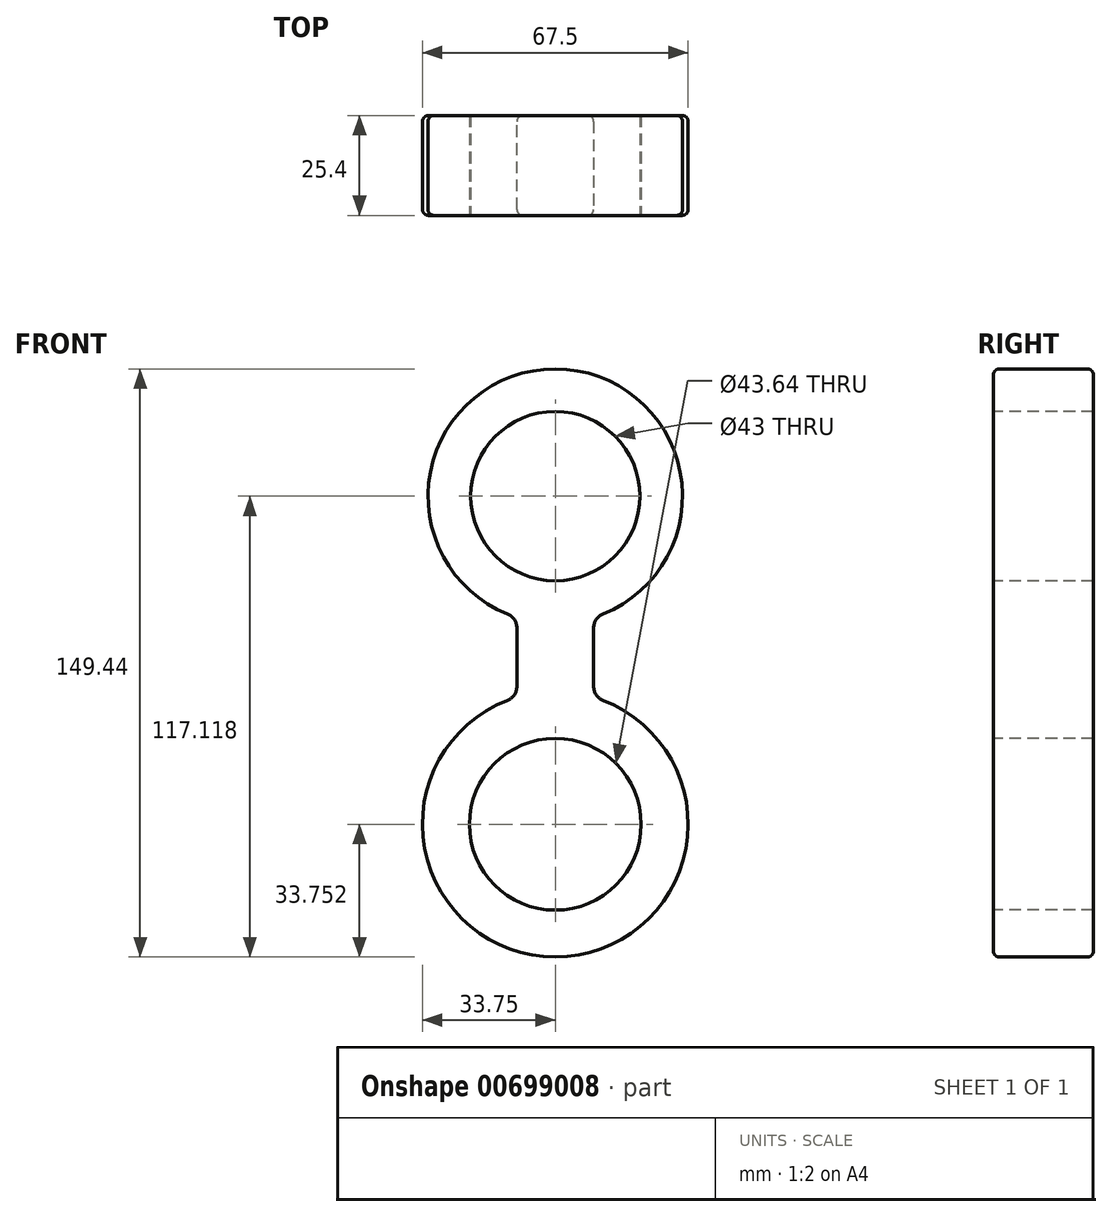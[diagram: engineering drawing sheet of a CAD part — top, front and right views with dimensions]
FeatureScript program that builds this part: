
annotation { "Feature Type Name" : "Feature", "Feature Type Description" : "" }
export const myFeature = defineFeature(function(context is Context, id is Id, definition is map)
    precondition{}
    {
        {
            var Q0;
            Q0=qCreatedBy(makeId("Front.planeOp"),FACE);
            var sketch = newSketch(context, id + "F0", { "sketchPlane" : qUnion([Q0])});
            skCircle(sketch, "E0", {"center": v(0, -42.15) * mm, "radius": 33.75 * mm});
            skCircle(sketch, "E1", {"center": v(0, -42.15) * mm, "radius": 21.82 * mm});
            skSolve(sketch);
        }
        {
            var Q0;
            Q0=makeQuery(id+"F0.imprint","IMPRINT",FACE,{"disambiguationData":[TD([[makeQuery(id+"F0.imprint","IMPRINT",EDGE,{"derivedFrom":sQuery(id+"F0.wireOp",EDGE,"E0")}),1.0]])]});
            var sketch = newSketch(context, id + "F1", { "sketchPlane" : qUnion([Q0])});
            skSolve(sketch);
        }
        {
            var Q0;
            Q0=makeQuery(id+"F1.imprint","IMPRINT",FACE,{"disambiguationData":[TD([[makeQuery(id+"F1.imprint","IMPRINT",EDGE,{"derivedFrom":makeQuery(id+"F0.imprint","IMPRINT",EDGE,{"derivedFrom":sQuery(id+"F0.wireOp",EDGE,"E0")})}),1.0]])]});
            var sketch = newSketch(context, id + "F2", { "sketchPlane" : qUnion([Q0])});
            skLineSegment(sketch, "E2.bottom", {"start": v(9.75, 16.05) * mm, "end": v(-9.75, 16.05) * mm});
            skLineSegment(sketch, "E2.top", {"start": v(9.75, -16.05) * mm, "end": v(-9.75, -16.05) * mm});
            skLineSegment(sketch, "E2.left", {"start": v(9.75, 16.05) * mm, "end": v(9.75, -16.05) * mm});
            skLineSegment(sketch, "E2.right", {"start": v(-9.75, 16.05) * mm, "end": v(-9.75, -16.05) * mm});
            skPoint(sketch, "E2.middle", {"position": v(0, 0) * mm});
            skSolve(sketch);
        }
        {
            var Q0;
            {var subQ1=sQuery(id+"F2.wireOp",EDGE,"E2.top");Q0=makeQuery(id+"F2.imprint","IMPRINT",FACE,{"disambiguationData":[TD([[makeQuery(id+"F2.imprint","IMPRINT",EDGE,{"derivedFrom":subQ1}),1.0]])]});}
            var Q1;
            {var subQ0=sQuery(id+"F2.wireOp",EDGE,"E2.bottom");Q1=makeQuery(id+"F2.imprint","IMPRINT",FACE,{"disambiguationData":[TD([[makeQuery(id+"F2.imprint","IMPRINT",EDGE,{"derivedFrom":subQ0}),1.0]])]});}
            var Q2;
            {var subQ0=sQuery(id+"F2.wireOp",EDGE,"E2.top");Q2=makeQuery(id+"F2.imprint","IMPRINT",FACE,{"disambiguationData":[TD([[makeQuery(id+"F2.imprint","IMPRINT",EDGE,{"derivedFrom":subQ0}),-1.0]])]});}
            extrude(context, id + "F3", {"entities" : qUnion([Q0, Q1, Q2]), "oppositeDirection" : true, "depth" : 25.4 * mm, "offsetDistance" : 25.4 * mm});
        }
        {
            var Q0;
            Q0=qCreatedBy(makeId("Front.planeOp"),FACE);
            var sketch = newSketch(context, id + "F4", { "sketchPlane" : qUnion([Q0])});
            skCircle(sketch, "E3", {"center": v(0, 41.22) * mm, "radius": 32.32 * mm});
            skCircle(sketch, "E4", {"center": v(0, 41.22) * mm, "radius": 21.5 * mm});
            skSolve(sketch);
        }
        {
            var Q0;
            Q0=makeQuery(id+"F4.imprint","IMPRINT",FACE,{"disambiguationData":[TD([[makeQuery(id+"F4.imprint","IMPRINT",EDGE,{"derivedFrom":sQuery(id+"F4.wireOp",EDGE,"E3")}),1.0]])]});
            extrude(context, id + "F5", {"entities" : qUnion([Q0]), "operationType" : NewBodyOperationType.ADD, "oppositeDirection" : true, "depth" : 25.4 * mm, "offsetDistance" : 25.4 * mm});
        }
        {
            var Q0;
            Q0=makeQuery(id+"F3.opExtrude","SWEPT_EDGE",EDGE,{"disambiguationData":[OSD([sQuery(id+"F0.wireOp",EDGE,"E0"),sQuery(id+"F2.wireOp",EDGE,"E2.right")])]});
            var Q1;
            Q1=makeQuery(id+"F5.boolean.opBoolean","INTERSECT",EDGE,{"derivedFrom":[makeQuery(id+"F3.opExtrude","SWEPT_FACE",FACE,{"disambiguationData":[OSD([sQuery(id+"F2.wireOp",EDGE,"E2.right")])]}),makeQuery(id+"F5.opExtrude","SWEPT_FACE",FACE,{"disambiguationData":[OSD([sQuery(id+"F4.wireOp",EDGE,"E3")])]})]});
            var Q2;
            Q2=makeQuery(id+"F5.boolean.opBoolean","INTERSECT",EDGE,{"derivedFrom":[makeQuery(id+"F3.opExtrude","SWEPT_FACE",FACE,{"disambiguationData":[OSD([sQuery(id+"F2.wireOp",EDGE,"E2.left")])]}),makeQuery(id+"F5.opExtrude","SWEPT_FACE",FACE,{"disambiguationData":[OSD([sQuery(id+"F4.wireOp",EDGE,"E3")])]})]});
            var Q3;
            Q3=makeQuery(id+"F3.opExtrude","SWEPT_EDGE",EDGE,{"disambiguationData":[OSD([sQuery(id+"F0.wireOp",EDGE,"E0"),sQuery(id+"F2.wireOp",EDGE,"E2.left")])]});
            fillet(context, id + "F6", {"entities" : qUnion([Q0, Q1, Q2, Q3]), "radius" : 3.8 * mm, "tangentPropagation" : true, "allowEdgeOverflow" : false});
        }
        {
            var Q0;
            Q0=makeQuery(id+"F3.opExtrude","SWEPT_FACE",FACE,{"disambiguationData":[OSD([sQuery(id+"F2.wireOp",EDGE,"E2.right")])]});
            var sketch = newSketch(context, id + "F7", { "sketchPlane" : qUnion([Q0])});
            skSolve(sketch);
        }
        {
            var Q0;
            Q0=makeQuery(id+"F3.opExtrude","SWEPT_FACE",FACE,{"disambiguationData":[OSD([sQuery(id+"F0.wireOp",EDGE,"E0")])]});
            var Q1;
            Q1=makeQuery(id+"F6.opFillet","BLEND_FACE",FACE,{"disambiguationData":[OSD([sQuery(id+"F0.wireOp",EDGE,"E0"),sQuery(id+"F2.wireOp",EDGE,"E2.left")])]});
            var Q2;
            Q2=makeQuery(id+"F6.opFillet","BLEND_FACE",FACE,{"disambiguationData":[OSD([sQuery(id+"F0.wireOp",EDGE,"E0"),sQuery(id+"F2.wireOp",EDGE,"E2.right")])]});
            var Q3;
            Q3=makeQuery(id+"F6.opFillet","BLEND_FACE",FACE,{"disambiguationData":[OSD([sQuery(id+"F2.wireOp",EDGE,"E2.left"),sQuery(id+"F4.wireOp",EDGE,"E3")])]});
            var Q4;
            Q4=makeQuery(id+"F5.opExtrude","SWEPT_FACE",FACE,{"disambiguationData":[OSD([sQuery(id+"F4.wireOp",EDGE,"E3")])]});
            var Q5;
            Q5=makeQuery(id+"F6.opFillet","BLEND_FACE",FACE,{"disambiguationData":[OSD([sQuery(id+"F2.wireOp",EDGE,"E2.right"),sQuery(id+"F4.wireOp",EDGE,"E3")])]});
            fillet(context, id + "F8", {"entities" : qUnion([Q0, Q1, Q2, Q3, Q4, Q5]), "radius" : 1.52 * mm, "tangentPropagation" : true, "allowEdgeOverflow" : false});
        }
    });
